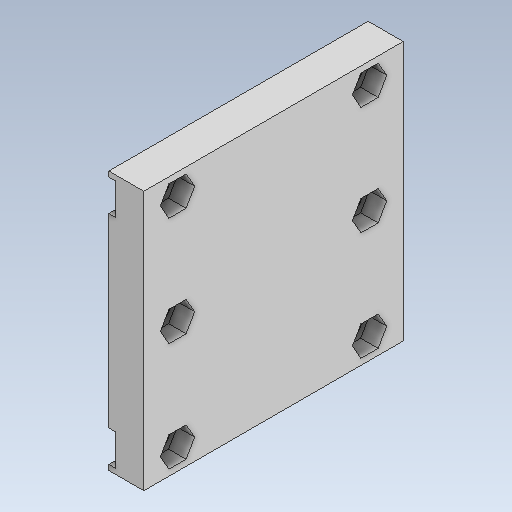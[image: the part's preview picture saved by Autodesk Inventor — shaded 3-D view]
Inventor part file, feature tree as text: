
AUTODESK INVENTOR PART (.ipt)
format: ipt  version: 2020 (Build 240168000, 168)  size: 197,120 bytes
history: native  units: mm
features: extrude x4, sketch x3, other x1
ambient origin geometry x8: Origin, YZ Plane, XZ Plane, XY Plane, X Axis, Y Axis, Z Axis, Center Point
bodies: Body1 (feature_tree)
feature tree (8):
  other  "Bryła1"
  extrude  "Wyciągnięcie proste1"  Depth=74.0mm
  sketch  "Szkic2"
  extrude  "Wyciągnięcie proste2"  Depth=74.0mm
  extrude  "Wyciągnięcie proste3"  Depth=10.0mm TaperAngle=0.0deg
  extrude  "Wyciągnięcie proste4"  Depth=6.0mm
  sketch  "Szkic1"
  sketch  "Szkic3"
